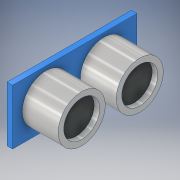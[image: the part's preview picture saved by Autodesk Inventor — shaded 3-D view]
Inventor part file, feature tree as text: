
AUTODESK INVENTOR PART (.ipt)
format: ipt  version: 2018 (Build 220112000, 112)  size: 142,336 bytes
history: native  units: in
note: dims shown in document units (in); Inventor stores cm internally (conversion verified against a paired STEP export)
features: extrude x3, sketch x3
ambient origin geometry x8: Origin, YZ Plane, XZ Plane, XY Plane, X Axis, Y Axis, Z Axis, Center Point
bodies: Solid1 (feature_tree)
feature tree (6):
  extrude  "Extrusion1"  Depth=0.7874in
  extrude  "Extrusion2"  Depth=0.0787in
  extrude  "Extrusion3"  Depth=0.3937in
  sketch  "Sketch1"  dims[d0=1.7717in d1=0.7874in]
  sketch  "Sketch2"  dims[d2=0.0787in d3=0.0in d4=0.6693in]
  sketch  "Sketch3"  dims[d5=0.3937in d6=0.3937in d7=0.4724in d8=0.4724in d9=0.5118in d10=0.0in d11=0.5118in d12=0.0787in d13=0.0in]
